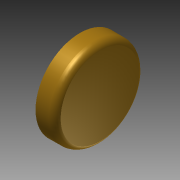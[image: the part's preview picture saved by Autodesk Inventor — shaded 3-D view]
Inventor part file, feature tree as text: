
AUTODESK INVENTOR PART (.ipt)
format: ipt  version: 2011 SP1 (Build 150282100, 282)  size: 145,920 bytes
history: native  units: mm
features: other x1, revolve x1, shell x1, sketch x1
ambient origin geometry x8: Origin, YZ Plane, XZ Plane, XY Plane, X Axis, Y Axis, Z Axis, Center Point
feature tree (4):
  other  "Твердое тело1"
  revolve  "Вращение1"
  shell  "Оболочка1"  Thickness=90.0deg
  sketch  "Эскиз1"
